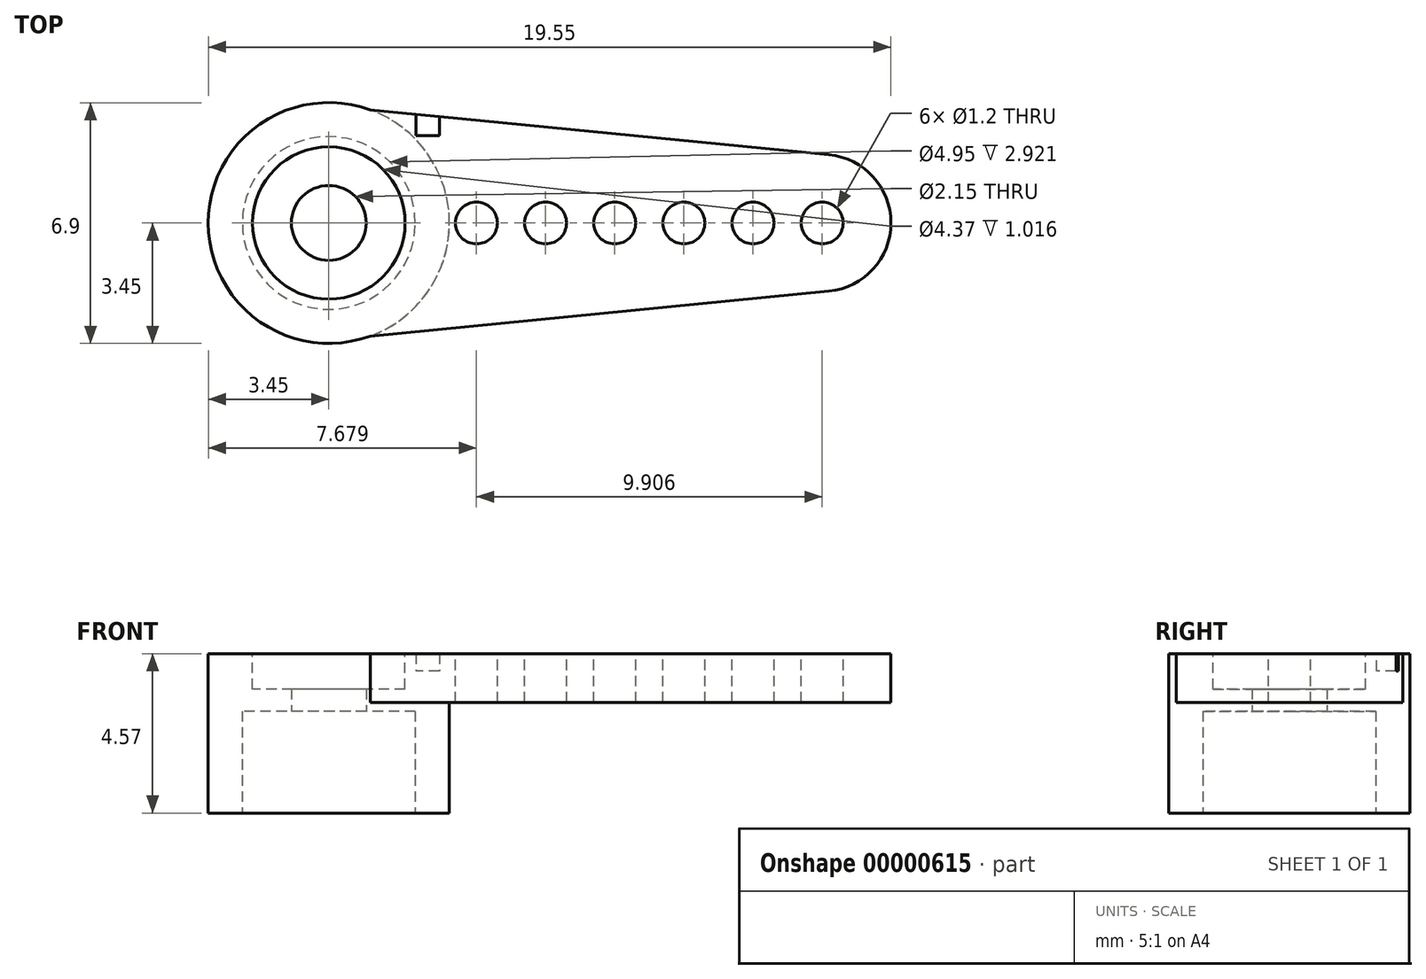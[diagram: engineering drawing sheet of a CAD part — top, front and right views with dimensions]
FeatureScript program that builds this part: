
annotation { "Feature Type Name" : "Feature", "Feature Type Description" : "" }
export const myFeature = defineFeature(function(context is Context, id is Id, definition is map)
    precondition{}
    {
        {
            var Q0;
            Q0=qCreatedBy(makeId("Top.planeOp"),FACE);
            var sketch = newSketch(context, id + "F0", { "sketchPlane" : qUnion([Q0])});
            skCircle(sketch, "E0", {"center": v(0, 0) * mm, "radius": 3.45 * mm});
            skCircle(sketch, "E1", {"center": v(0, 0) * mm, "radius": 2.48 * mm});
            skSolve(sketch);
        }
        {
            var Q0;
            Q0=makeQuery(id+"F0.imprint","IMPRINT",FACE,{"disambiguationData":[TD([[makeQuery(id+"F0.imprint","IMPRINT",EDGE,{"derivedFrom":sQuery(id+"F0.wireOp",EDGE,"E0")}),1.0]])]});
            extrude(context, id + "F1", {"entities" : qUnion([Q0]), "depth" : 2.92 * mm});
        }
        {
            var Q0;
            Q0=makeQuery(id+"F1.opExtrude","CAP_FACE",FACE,{"disambiguationData":[OSD([sQuery(id+"F0.wireOp",EDGE,"E0"),sQuery(id+"F0.wireOp",EDGE,"E1")])],"isStart":false});
            var sketch = newSketch(context, id + "F2", { "sketchPlane" : qUnion([Q0])});
            skCircle(sketch, "E2", {"center": v(0, 0) * mm, "radius": 3.45 * mm});
            skCircle(sketch, "E3", {"center": v(0, 0) * mm, "radius": 1.07 * mm});
            skSolve(sketch);
        }
        {
            var Q0;
            {Q0=qUnion([makeQuery(id+"F2.imprint","IMPRINT",FACE,{"disambiguationData":[TD([[makeQuery(id+"F2.imprint","IMPRINT",EDGE,{"derivedFrom":sQuery(id+"F2.wireOp",EDGE,"E2")}),1.0]])]}),makeQuery(id+"F2.imprint","IMPRINT",FACE,{"disambiguationData":[TD([[makeQuery(id+"F2.imprint","IMPRINT",EDGE,{"derivedFrom":sQuery(id+"F2.wireOp",EDGE,"E3")}),-1.0]])]})]);}
            extrude(context, id + "F3", {"entities" : qUnion([Q0]), "operationType" : NewBodyOperationType.ADD, "depth" : 0.64 * mm});
        }
        {
            var Q0;
            Q0=makeQuery(id+"F3.opExtrude","CAP_FACE",FACE,{"disambiguationData":[OSD([sQuery(id+"F2.wireOp",EDGE,"E2"),sQuery(id+"F2.wireOp",EDGE,"E3")])],"isStart":false});
            var sketch = newSketch(context, id + "F4", { "sketchPlane" : qUnion([Q0])});
            skCircle(sketch, "E4", {"center": v(0, 0) * mm, "radius": 3.45 * mm});
            skCircle(sketch, "E5", {"center": v(0, 0) * mm, "radius": 2.18 * mm});
            skSolve(sketch);
        }
        {
            var Q0;
            {var subQ0=makeQuery(id+"F4.imprint","IMPRINT",EDGE,{"derivedFrom":sQuery(id+"F4.wireOp",EDGE,"E5")});var subQ1=makeQuery(id+"F4.imprint","IMPRINT",EDGE,{"derivedFrom":makeQuery(id+"F3.opExtrude","CAP_EDGE",EDGE,{"disambiguationData":[OSD([sQuery(id+"F2.wireOp",EDGE,"E3")])],"isStart":false})});Q0=qUnion([makeQuery(id+"F4.imprint","IMPRINT",FACE,{"disambiguationData":[TD([[makeQuery(id+"F4.imprint","IMPRINT",EDGE,{"derivedFrom":sQuery(id+"F4.wireOp",EDGE,"E4")}),1.0]])]}),makeQuery(id+"F4.imprint","IMPRINT",FACE,{"disambiguationData":[TD([[subQ1,1.0]])]}),makeQuery(id+"F4.imprint","IMPRINT",FACE,{"disambiguationData":[TD([[subQ0,1.0]])]})]);}
            extrude(context, id + "F5", {"entities" : qUnion([Q0]), "operationType" : NewBodyOperationType.ADD, "depth" : 1.02 * mm});
        }
        {
            var Q0;
            Q0=makeQuery(id+"F5.opExtrude","CAP_FACE",FACE,{"disambiguationData":[OSD([sQuery(id+"F4.wireOp",EDGE,"E4")])],"isStart":false});
            var sketch = newSketch(context, id + "F6", { "sketchPlane" : qUnion([Q0])});
            skLineSegment(sketch, "E6", {"start": v(1.19, 3.24) * mm, "end": v(1.19, -3.24) * mm});
            skArc(sketch, "E7", {"start": v(14.33, -1.96) * mm, "mid": v(16.1, 0) * mm, "end": v(14.33, 1.96) * mm});
            skLineSegment(sketch, "E8", {"start": v(1.19, 3.24) * mm, "end": v(14.33, 1.96) * mm});
            skLineSegment(sketch, "E9", {"start": v(14.33, -1.96) * mm, "end": v(1.19, -3.24) * mm});
            skSolve(sketch);
        }
        {
            var Q0;
            {var subQ1=sQuery(id+"F6.wireOp",EDGE,"E6");Q0=qUnion([makeQuery(id+"F6.imprint","IMPRINT",FACE,{"disambiguationData":[TD([[makeQuery(id+"F6.imprint","IMPRINT",EDGE,{"derivedFrom":sQuery(id+"F6.wireOp",EDGE,"E7")}),1.0]])]}),makeQuery(id+"F6.imprint","IMPRINT",FACE,{"disambiguationData":[TD([[makeQuery(id+"F6.imprint","IMPRINT",EDGE,{"derivedFrom":subQ1}),1.0]])]})]);}
            extrude(context, id + "F7", {"entities" : qUnion([Q0]), "operationType" : NewBodyOperationType.ADD, "oppositeDirection" : true, "depth" : 1.4 * mm});
        }
        {
            var Q0;
            Q0=makeQuery(id+"F7.boolean.opBoolean","MERGE",FACE,{"derivedFrom":[makeQuery(id+"F5.opExtrude","CAP_FACE",FACE,{"disambiguationData":[OSD([sQuery(id+"F4.wireOp",EDGE,"E4")])],"isStart":false}),makeQuery(id+"F7.opExtrude","CAP_FACE",FACE,{"disambiguationData":[OSD([sQuery(id+"F6.wireOp",EDGE,"E6"),sQuery(id+"F6.wireOp",EDGE,"E7"),sQuery(id+"F6.wireOp",EDGE,"E8"),sQuery(id+"F6.wireOp",EDGE,"E9")])],"isStart":true})]});
            var sketch = newSketch(context, id + "F8", { "sketchPlane" : qUnion([Q0])});
            skCircle(sketch, "E10", {"center": v(0, 0) * mm, "radius": 2.18 * mm});
            skSolve(sketch);
        }
        {
            var Q0;
            Q0=makeQuery(id+"F8.imprint","IMPRINT",FACE,{"disambiguationData":[TD([[makeQuery(id+"F8.imprint","IMPRINT",EDGE,{"derivedFrom":sQuery(id+"F8.wireOp",EDGE,"E10")}),1.0]])]});
            extrude(context, id + "F9", {"entities" : qUnion([Q0]), "operationType" : NewBodyOperationType.REMOVE, "oppositeDirection" : true, "depth" : 1.02 * mm});
        }
        {
            var Q0;
            Q0=makeQuery(id+"F7.boolean.opBoolean","MERGE",FACE,{"derivedFrom":[makeQuery(id+"F5.opExtrude","CAP_FACE",FACE,{"disambiguationData":[OSD([sQuery(id+"F4.wireOp",EDGE,"E4")])],"isStart":false}),makeQuery(id+"F7.opExtrude","CAP_FACE",FACE,{"disambiguationData":[OSD([sQuery(id+"F6.wireOp",EDGE,"E6"),sQuery(id+"F6.wireOp",EDGE,"E7"),sQuery(id+"F6.wireOp",EDGE,"E8"),sQuery(id+"F6.wireOp",EDGE,"E9")])],"isStart":true})]});
            var sketch = newSketch(context, id + "F10", { "sketchPlane" : qUnion([Q0])});
            skCircle(sketch, "E11", {"center": v(14.14, 0) * mm, "radius": 0.6 * mm});
            skCircle(sketch, "E12", {"center": v(12.15, 0) * mm, "radius": 0.6 * mm});
            skCircle(sketch, "E13", {"center": v(10.17, 0) * mm, "radius": 0.6 * mm});
            skCircle(sketch, "E14", {"center": v(8.2, 0) * mm, "radius": 0.6 * mm});
            skCircle(sketch, "E15", {"center": v(6.21, 0) * mm, "radius": 0.6 * mm});
            skCircle(sketch, "E16", {"center": v(4.23, 0) * mm, "radius": 0.6 * mm});
            skSolve(sketch);
        }
        {
            var Q0;
            {Q0=qUnion([makeQuery(id+"F10.imprint","IMPRINT",FACE,{"disambiguationData":[TD([[makeQuery(id+"F10.imprint","IMPRINT",EDGE,{"derivedFrom":sQuery(id+"F10.wireOp",EDGE,"E11")}),1.0]])]}),makeQuery(id+"F10.imprint","IMPRINT",FACE,{"disambiguationData":[TD([[makeQuery(id+"F10.imprint","IMPRINT",EDGE,{"derivedFrom":sQuery(id+"F10.wireOp",EDGE,"E12")}),1.0]])]}),makeQuery(id+"F10.imprint","IMPRINT",FACE,{"disambiguationData":[TD([[makeQuery(id+"F10.imprint","IMPRINT",EDGE,{"derivedFrom":sQuery(id+"F10.wireOp",EDGE,"E13")}),1.0]])]}),makeQuery(id+"F10.imprint","IMPRINT",FACE,{"disambiguationData":[TD([[makeQuery(id+"F10.imprint","IMPRINT",EDGE,{"derivedFrom":sQuery(id+"F10.wireOp",EDGE,"E14")}),1.0]])]}),makeQuery(id+"F10.imprint","IMPRINT",FACE,{"disambiguationData":[TD([[makeQuery(id+"F10.imprint","IMPRINT",EDGE,{"derivedFrom":sQuery(id+"F10.wireOp",EDGE,"E15")}),1.0]])]}),makeQuery(id+"F10.imprint","IMPRINT",FACE,{"disambiguationData":[TD([[makeQuery(id+"F10.imprint","IMPRINT",EDGE,{"derivedFrom":sQuery(id+"F10.wireOp",EDGE,"E16")}),1.0]])]})]);}
            extrude(context, id + "F11", {"entities" : qUnion([Q0]), "operationType" : NewBodyOperationType.REMOVE, "endBound" : BoundingType.THROUGH_ALL, "oppositeDirection" : true, "depth" : 25.4 * mm});
        }
        {
            var Q0;
            Q0=makeQuery(id+"F7.boolean.opBoolean","MERGE",FACE,{"derivedFrom":[makeQuery(id+"F5.opExtrude","CAP_FACE",FACE,{"disambiguationData":[OSD([sQuery(id+"F4.wireOp",EDGE,"E4")])],"isStart":false}),makeQuery(id+"F7.opExtrude","CAP_FACE",FACE,{"disambiguationData":[OSD([sQuery(id+"F6.wireOp",EDGE,"E6"),sQuery(id+"F6.wireOp",EDGE,"E7"),sQuery(id+"F6.wireOp",EDGE,"E8"),sQuery(id+"F6.wireOp",EDGE,"E9")])],"isStart":true})]});
            var sketch = newSketch(context, id + "F12", { "sketchPlane" : qUnion([Q0])});
            skLineSegment(sketch, "E17.bottom", {"start": v(2.5, 3.2) * mm, "end": v(3.17, 3.2) * mm});
            skLineSegment(sketch, "E17.top", {"start": v(2.5, 2.5) * mm, "end": v(3.17, 2.5) * mm});
            skLineSegment(sketch, "E17.left", {"start": v(2.5, 3.2) * mm, "end": v(2.5, 2.5) * mm});
            skLineSegment(sketch, "E17.right", {"start": v(3.17, 3.2) * mm, "end": v(3.17, 2.5) * mm});
            skSolve(sketch);
        }
        {
            var Q0;
            {var subQ6=sQuery(id+"F12.wireOp",EDGE,"E17.bottom");var subQ7=sQuery(id+"F12.wireOp",EDGE,"E17.top");Q0=qUnion([makeQuery(id+"F12.imprint","IMPRINT",FACE,{"disambiguationData":[TD([[makeQuery(id+"F12.imprint","IMPRINT",EDGE,{"derivedFrom":subQ6}),-1.0]])]}),makeQuery(id+"F12.imprint","IMPRINT",FACE,{"disambiguationData":[TD([[makeQuery(id+"F12.imprint","IMPRINT",EDGE,{"derivedFrom":subQ7}),1.0]])]})]);}
            extrude(context, id + "F13", {"entities" : qUnion([Q0]), "operationType" : NewBodyOperationType.REMOVE, "oppositeDirection" : true, "depth" : .5 * mm});
        }
    });
